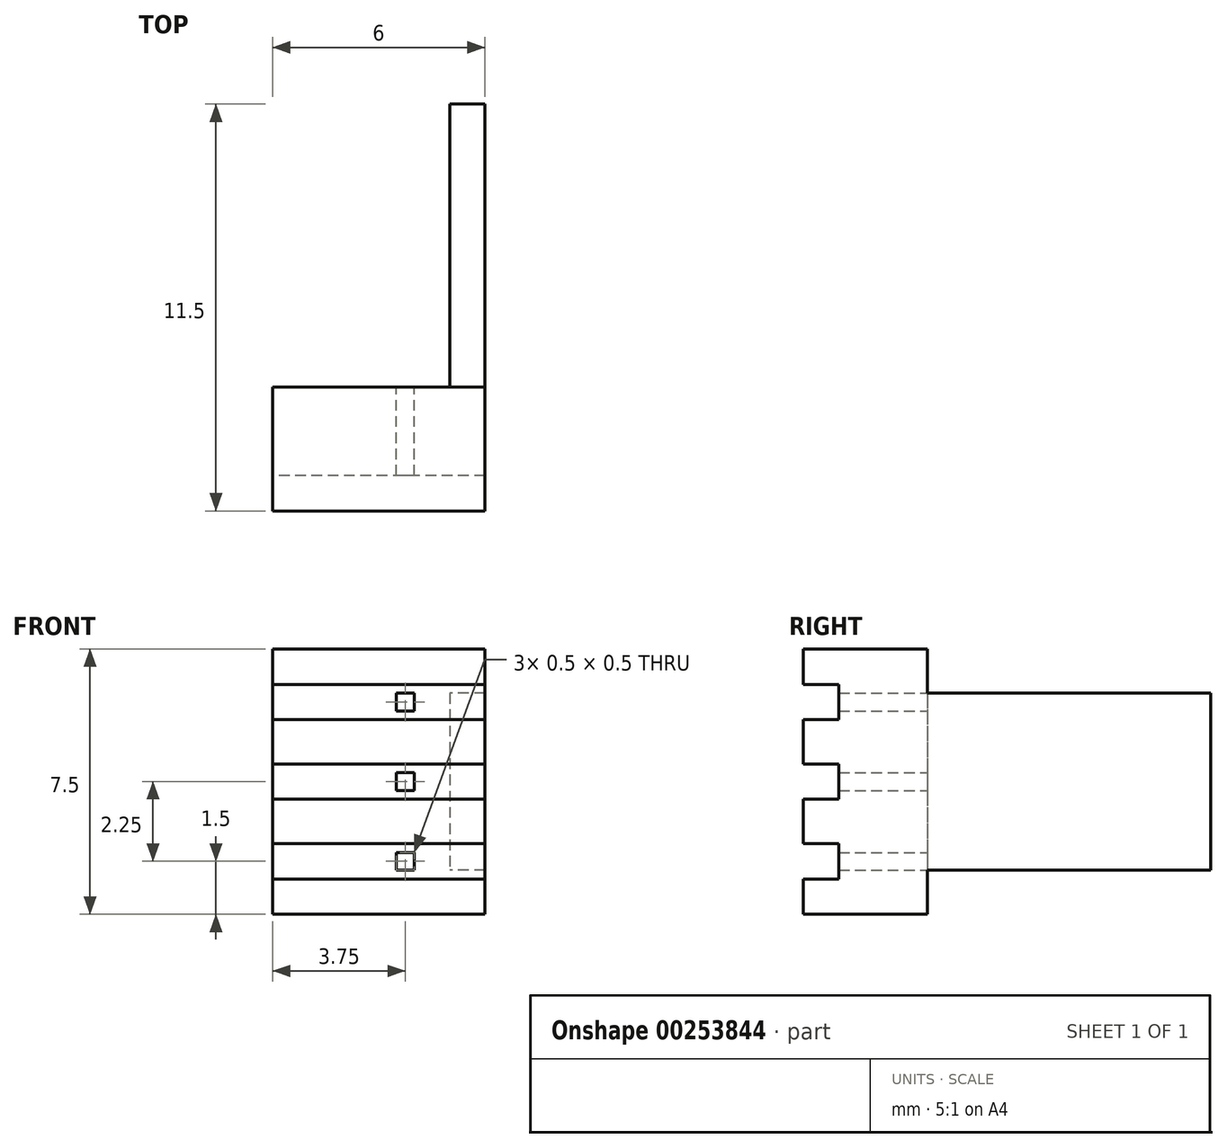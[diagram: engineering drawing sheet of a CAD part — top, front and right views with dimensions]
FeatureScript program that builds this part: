
annotation { "Feature Type Name" : "Feature", "Feature Type Description" : "" }
export const myFeature = defineFeature(function(context is Context, id is Id, definition is map)
    precondition{}
    {
        {
            var Q0;
            Q0=qCreatedBy(makeId("Top.planeOp"),FACE);
            var sketch = newSketch(context, id + "F0", { "sketchPlane" : qUnion([Q0])});
            skLineSegment(sketch, "E0.bottom", {"start": v(0, 0) * mm, "end": v(6, 0) * mm});
            skLineSegment(sketch, "E0.top", {"start": v(5, 11.5) * mm, "end": v(6, 11.5) * mm});
            skLineSegment(sketch, "E0.left", {"start": v(0, 0) * mm, "end": v(0, 3.5) * mm});
            skLineSegment(sketch, "E0.right", {"start": v(6, 0) * mm, "end": v(6, 11.5) * mm});
            skLineSegment(sketch, "E1", {"start": v(5, 11.5) * mm, "end": v(5, 3.5) * mm});
            skLineSegment(sketch, "E2", {"start": v(5, 3.5) * mm, "end": v(0, 3.5) * mm});
            skSolve(sketch);
        }
        {
            var Q0;
            Q0 = qSketchRegion(id + "F0", true);
            extrude(context, id + "F1", {"entities" : qUnion([Q0]), "depth" : 7.5 * mm});
        }
        {
            var Q0;
            Q0=makeQuery(id+"F1.opExtrude","SWEPT_FACE",FACE,{"disambiguationData":[OSD([sQuery(id+"F0.wireOp",EDGE,"E1")])]});
            var sketch = newSketch(context, id + "F2", { "sketchPlane" : qUnion([Q0])});
            skLineSegment(sketch, "E3.bottom", {"start": v(-11.5, 0) * mm, "end": v(-3.5, 0) * mm});
            skLineSegment(sketch, "E3.top", {"start": v(-11.5, 1.25) * mm, "end": v(-3.5, 1.25) * mm});
            skLineSegment(sketch, "E3.left", {"start": v(-11.5, 0) * mm, "end": v(-11.5, 1.25) * mm});
            skLineSegment(sketch, "E3.right", {"start": v(-3.5, 0) * mm, "end": v(-3.5, 1.25) * mm});
            skLineSegment(sketch, "E4.bottom", {"start": v(-11.5, 7.5) * mm, "end": v(-3.5, 7.5) * mm});
            skLineSegment(sketch, "E4.top", {"start": v(-11.5, 6.25) * mm, "end": v(-3.5, 6.25) * mm});
            skLineSegment(sketch, "E4.left", {"start": v(-11.5, 7.5) * mm, "end": v(-11.5, 6.25) * mm});
            skLineSegment(sketch, "E4.right", {"start": v(-3.5, 7.5) * mm, "end": v(-3.5, 6.25) * mm});
            skSolve(sketch);
        }
        {
            var Q0;
            Q0 = qSketchRegion(id + "F2", true);
            extrude(context, id + "F3", {"entities" : qUnion([Q0]), "operationType" : NewBodyOperationType.REMOVE, "oppositeDirection" : true, "depth" : 25 * mm});
        }
        {
            var Q0;
            Q0=makeQuery(id+"F3.boolean.opBoolean","MERGE",FACE,{"derivedFrom":[makeQuery(id+"F1.opExtrude","SWEPT_FACE",FACE,{"disambiguationData":[OSD([sQuery(id+"F0.wireOp",EDGE,"E2")])]}),makeQuery(id+"F3.opExtrude","SWEPT_FACE",FACE,{"disambiguationData":[OSD([sQuery(id+"F2.wireOp",EDGE,"E3.right")])]}),makeQuery(id+"F3.opExtrude","SWEPT_FACE",FACE,{"disambiguationData":[OSD([sQuery(id+"F2.wireOp",EDGE,"E4.right")])]})]});
            var sketch = newSketch(context, id + "F4", { "sketchPlane" : qUnion([Q0])});
            skLineSegment(sketch, "E5.bottom", {"start": v(-4, 6.25) * mm, "end": v(-3.5, 6.25) * mm});
            skLineSegment(sketch, "E5.top", {"start": v(-4, 1.25) * mm, "end": v(-3.5, 1.25) * mm});
            skLineSegment(sketch, "E5.left", {"start": v(-4, 6.25) * mm, "end": v(-4, 5.75) * mm});
            skLineSegment(sketch, "E5.right", {"start": v(-3.5, 6.25) * mm, "end": v(-3.5, 5.75) * mm});
            skLineSegment(sketch, "E6", {"start": v(-4, 5.75) * mm, "end": v(-3.5, 5.75) * mm});
            skLineSegment(sketch, "E7", {"start": v(-4, 1.75) * mm, "end": v(-3.5, 1.75) * mm});
            skLineSegment(sketch, "E8", {"start": v(-4, 4) * mm, "end": v(-3.5, 4) * mm});
            skLineSegment(sketch, "E9", {"start": v(-4, 3.5) * mm, "end": v(-3.5, 3.5) * mm});
            skLineSegment(sketch, "E10.trimOffspring", {"start": v(-4, 4) * mm, "end": v(-4, 3.5) * mm});
            skLineSegment(sketch, "E11.trimOffspring", {"start": v(-3.5, 4) * mm, "end": v(-3.5, 3.5) * mm});
            skLineSegment(sketch, "E12.trimOffspring", {"start": v(-4, 1.75) * mm, "end": v(-4, 1.25) * mm});
            skLineSegment(sketch, "E13.trimOffspring", {"start": v(-3.5, 1.75) * mm, "end": v(-3.5, 1.25) * mm});
            skLineSegment(sketch, "E14", {"start": v(0, 3.75) * mm, "end": v(-5, 3.75) * mm, "construction": true});
            skPoint(sketch, "E14.endSnap0", {"position": v(0, 3.75) * mm});
            skSolve(sketch);
        }
        {
            var Q0;
            Q0 = qSketchRegion(id + "F4", true);
            var Q1;
            Q1=makeQuery(id+"F1.opExtrude","SWEPT_FACE",FACE,{"disambiguationData":[OSD([sQuery(id+"F0.wireOp",EDGE,"E0.top")])]});
            extrude(context, id + "F5", {"entities" : qUnion([Q0]), "operationType" : NewBodyOperationType.REMOVE, "oppositeDirection" : true, "endBoundEntityFace" : qUnion([Q1]), "depth" : 25 * mm});
        }
        {
            var Q0;
            Q0=makeQuery(id+"F1.opExtrude","SWEPT_FACE",FACE,{"disambiguationData":[OSD([sQuery(id+"F0.wireOp",EDGE,"E0.bottom")])]});
            var sketch = newSketch(context, id + "F6", { "sketchPlane" : qUnion([Q0])});
            skLineSegment(sketch, "E15.bottom", {"start": v(6, 6.5) * mm, "end": v(0, 6.5) * mm});
            skLineSegment(sketch, "E15.top", {"start": v(6, 5.5) * mm, "end": v(0, 5.5) * mm});
            skLineSegment(sketch, "E15.left", {"start": v(6, 6.5) * mm, "end": v(6, 5.5) * mm});
            skLineSegment(sketch, "E15.right", {"start": v(0, 6.5) * mm, "end": v(0, 5.5) * mm});
            skLineSegment(sketch, "E16.bottom", {"start": v(6, 4.25) * mm, "end": v(0, 4.25) * mm});
            skLineSegment(sketch, "E16.top", {"start": v(6, 3.25) * mm, "end": v(0, 3.25) * mm});
            skLineSegment(sketch, "E16.left", {"start": v(6, 4.25) * mm, "end": v(6, 3.25) * mm});
            skLineSegment(sketch, "E16.right", {"start": v(0, 4.25) * mm, "end": v(0, 3.25) * mm});
            skLineSegment(sketch, "E17.bottom", {"start": v(6, 2) * mm, "end": v(0, 2) * mm});
            skLineSegment(sketch, "E17.top", {"start": v(6, 1) * mm, "end": v(0, 1) * mm});
            skLineSegment(sketch, "E17.left", {"start": v(6, 2) * mm, "end": v(6, 1) * mm});
            skLineSegment(sketch, "E17.right", {"start": v(0, 2) * mm, "end": v(0, 1) * mm});
            skSolve(sketch);
        }
        {
            var Q0;
            Q0 = qSketchRegion(id + "F6", true);
            extrude(context, id + "F7", {"entities" : qUnion([Q0]), "operationType" : NewBodyOperationType.REMOVE, "oppositeDirection" : true, "depth" : 1 * mm});
        }
    });
